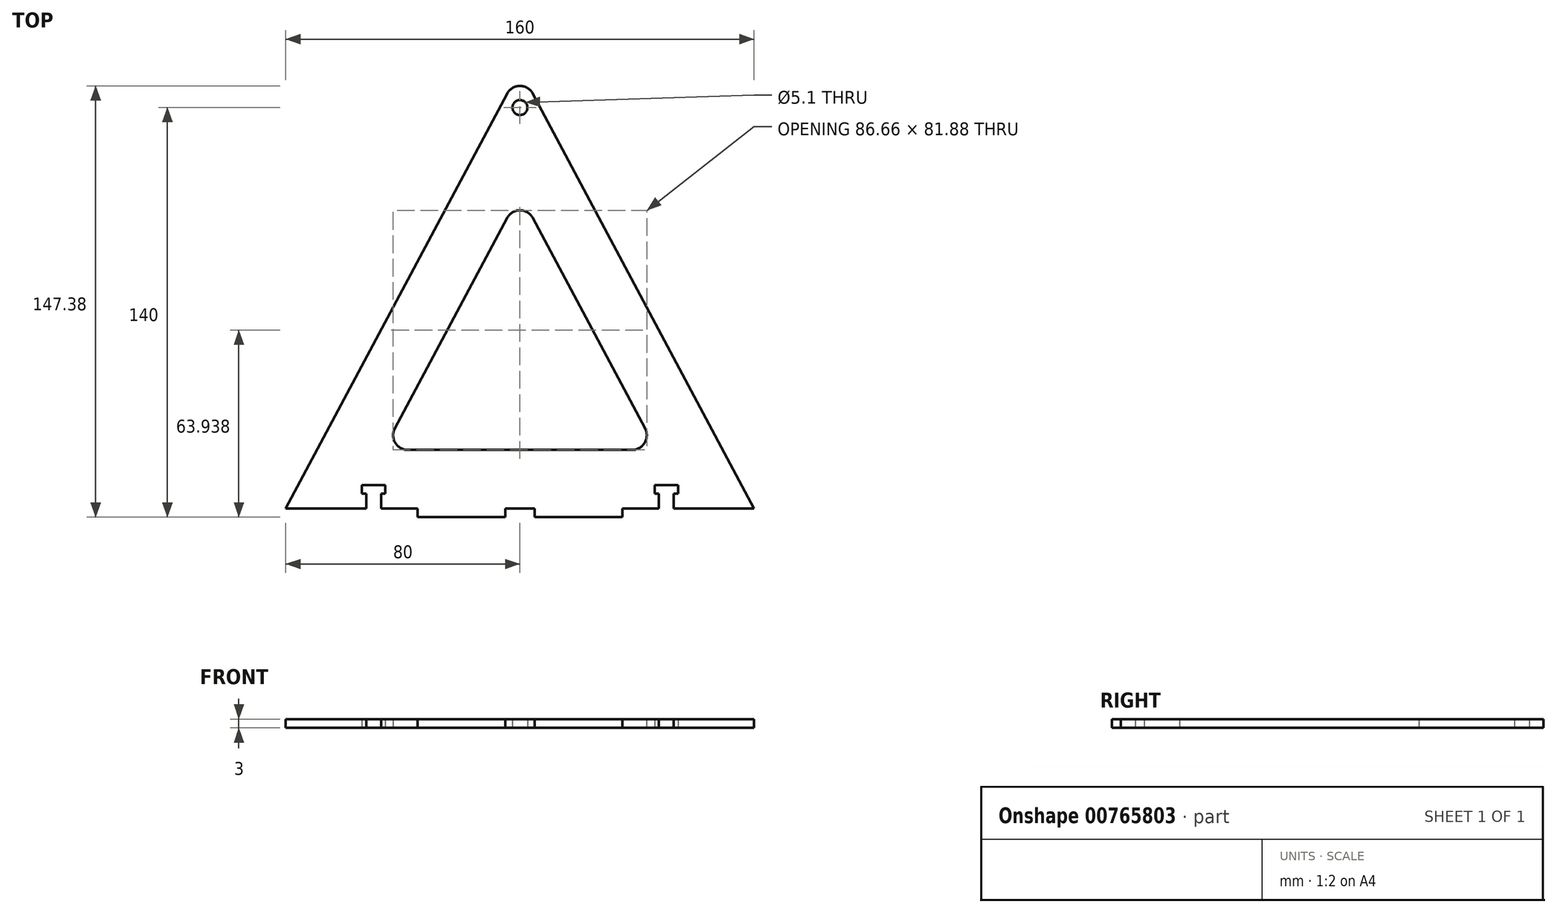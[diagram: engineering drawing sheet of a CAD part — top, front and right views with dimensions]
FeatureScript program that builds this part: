
annotation { "Feature Type Name" : "Feature", "Feature Type Description" : "" }
export const myFeature = defineFeature(function(context is Context, id is Id, definition is map)
    precondition{}
    {
        {
            var Q0;
            Q0=qCreatedBy(makeId("Top.planeOp"),FACE);
            var sketch = newSketch(context, id + "F0", { "sketchPlane" : qUnion([Q0])});
            skLineSegment(sketch, "E0", {"start": v(-80, 0) * mm, "end": v(0, 150) * mm});
            skLineSegment(sketch, "E1", {"start": v(-80, 0) * mm, "end": v(-35, 0) * mm});
            skLineSegment(sketch, "E2", {"start": v(-35, 0) * mm, "end": v(-35, -3) * mm});
            skLineSegment(sketch, "E3", {"start": v(-35, -3) * mm, "end": v(-5, -3) * mm});
            skLineSegment(sketch, "E4", {"start": v(-5, -3) * mm, "end": v(-5, 0) * mm});
            skLineSegment(sketch, "E5", {"start": v(-5, 0) * mm, "end": v(0, 0) * mm});
            skLineSegment(sketch, "E6.top", {"start": v(-52.55, 8) * mm, "end": v(-47.45, 8) * mm});
            skLineSegment(sketch, "E6.left", {"start": v(-52.55, 0) * mm, "end": v(-52.55, 8) * mm});
            skLineSegment(sketch, "E6.right", {"start": v(-47.45, 0) * mm, "end": v(-47.45, 8) * mm});
            skLineSegment(sketch, "E7.bottom", {"start": v(-50, 8) * mm, "end": v(-54, 8) * mm});
            skLineSegment(sketch, "E7.top", {"start": v(-50, 5) * mm, "end": v(-54, 5) * mm});
            skLineSegment(sketch, "E7.left", {"start": v(-50, 5) * mm, "end": v(-50, 8) * mm});
            skLineSegment(sketch, "E7.right", {"start": v(-54, 5) * mm, "end": v(-54, 8) * mm});
            skLineSegment(sketch, "E8.MirrorCS", {"start": v(-46, 5) * mm, "end": v(-46, 8) * mm});
            skLineSegment(sketch, "E9.MirrorCS", {"start": v(-50, 5) * mm, "end": v(-46, 5) * mm});
            skLineSegment(sketch, "E10.MirrorCS", {"start": v(-50, 8) * mm, "end": v(-46, 8) * mm});
            skLineSegment(sketch, "E11.MirrorCS", {"start": v(80, 0) * mm, "end": v(0, 150) * mm});
            skLineSegment(sketch, "E12.MirrorCS", {"start": v(50, 5) * mm, "end": v(50, 8) * mm});
            skLineSegment(sketch, "E13.MirrorCS", {"start": v(52.55, 8) * mm, "end": v(47.45, 8) * mm});
            skLineSegment(sketch, "E14.MirrorCS", {"start": v(54, 5) * mm, "end": v(54, 8) * mm});
            skLineSegment(sketch, "E15.MirrorCS", {"start": v(50, 5) * mm, "end": v(54, 5) * mm});
            skLineSegment(sketch, "E16.MirrorCS", {"start": v(50, 8) * mm, "end": v(54, 8) * mm});
            skLineSegment(sketch, "E17.MirrorCS", {"start": v(46, 5) * mm, "end": v(46, 8) * mm});
            skLineSegment(sketch, "E18.MirrorCS", {"start": v(50, 5) * mm, "end": v(46, 5) * mm});
            skLineSegment(sketch, "E19.MirrorCS", {"start": v(50, 8) * mm, "end": v(46, 8) * mm});
            skLineSegment(sketch, "E20.MirrorCS", {"start": v(5, 0) * mm, "end": v(0, 0) * mm});
            skLineSegment(sketch, "E21.MirrorCS", {"start": v(47.45, 0) * mm, "end": v(47.45, 8) * mm});
            skLineSegment(sketch, "E22.MirrorCS", {"start": v(52.55, 0) * mm, "end": v(52.55, 8) * mm});
            skLineSegment(sketch, "E23.MirrorCS", {"start": v(5, -3) * mm, "end": v(5, 0) * mm});
            skLineSegment(sketch, "E24.MirrorCS", {"start": v(35, 0) * mm, "end": v(35, -3) * mm});
            skLineSegment(sketch, "E25.MirrorCS", {"start": v(80, 0) * mm, "end": v(35, 0) * mm});
            skLineSegment(sketch, "E26.MirrorCS", {"start": v(35, -3) * mm, "end": v(5, -3) * mm});
            skCircle(sketch, "E27", {"center": v(0, 137) * mm, "radius": 2.55 * mm});
            skLineSegment(sketch, "E28", {"start": v(0, 20) * mm, "end": v(-46.67, 20) * mm});
            skLineSegment(sketch, "E29", {"start": v(-46.67, 20) * mm, "end": v(0, 107.5) * mm});
            skLineSegment(sketch, "E30.MirrorCS", {"start": v(46.67, 20) * mm, "end": v(0, 107.5) * mm});
            skLineSegment(sketch, "E31.MirrorCS", {"start": v(0, 20) * mm, "end": v(46.67, 20) * mm});
            skSolve(sketch);
        }
        {
            var Q0;
            {var subQ11=sQuery(id+"F0.wireOp",EDGE,"E0");Q0=makeQuery(id+"F0.imprint","IMPRINT",FACE,{"disambiguationData":[TD([[makeQuery(id+"F0.imprint","IMPRINT",EDGE,{"derivedFrom":subQ11}),-1.0]])]});}
            extrude(context, id + "F1", {"entities" : qUnion([Q0]), "depth" : 3 * mm, "offsetDistance" : 25 * mm});
        }
        {
            var Q0;
            Q0=makeQuery(id+"F1.opExtrude","SWEPT_EDGE",EDGE,{"disambiguationData":[OSD([sQuery(id+"F0.wireOp",EDGE,"E0"),sQuery(id+"F0.wireOp",EDGE,"E11.MirrorCS")])]});
            var Q1;
            Q1=makeQuery(id+"F1.opExtrude","SWEPT_EDGE",EDGE,{"disambiguationData":[OSD([sQuery(id+"F0.wireOp",EDGE,"E29"),sQuery(id+"F0.wireOp",EDGE,"E30.MirrorCS")])]});
            var Q2;
            Q2=makeQuery(id+"F1.opExtrude","SWEPT_EDGE",EDGE,{"disambiguationData":[OSD([sQuery(id+"F0.wireOp",EDGE,"E30.MirrorCS"),sQuery(id+"F0.wireOp",EDGE,"E31.MirrorCS")])]});
            var Q3;
            Q3=makeQuery(id+"F1.opExtrude","SWEPT_EDGE",EDGE,{"disambiguationData":[OSD([sQuery(id+"F0.wireOp",EDGE,"E28"),sQuery(id+"F0.wireOp",EDGE,"E29")])]});
            fillet(context, id + "F2", {"entities" : qUnion([Q0, Q1, Q2, Q3]), "radius" : 5 * mm, "tangentPropagation" : true, "allowEdgeOverflow" : false});
        }
    });
